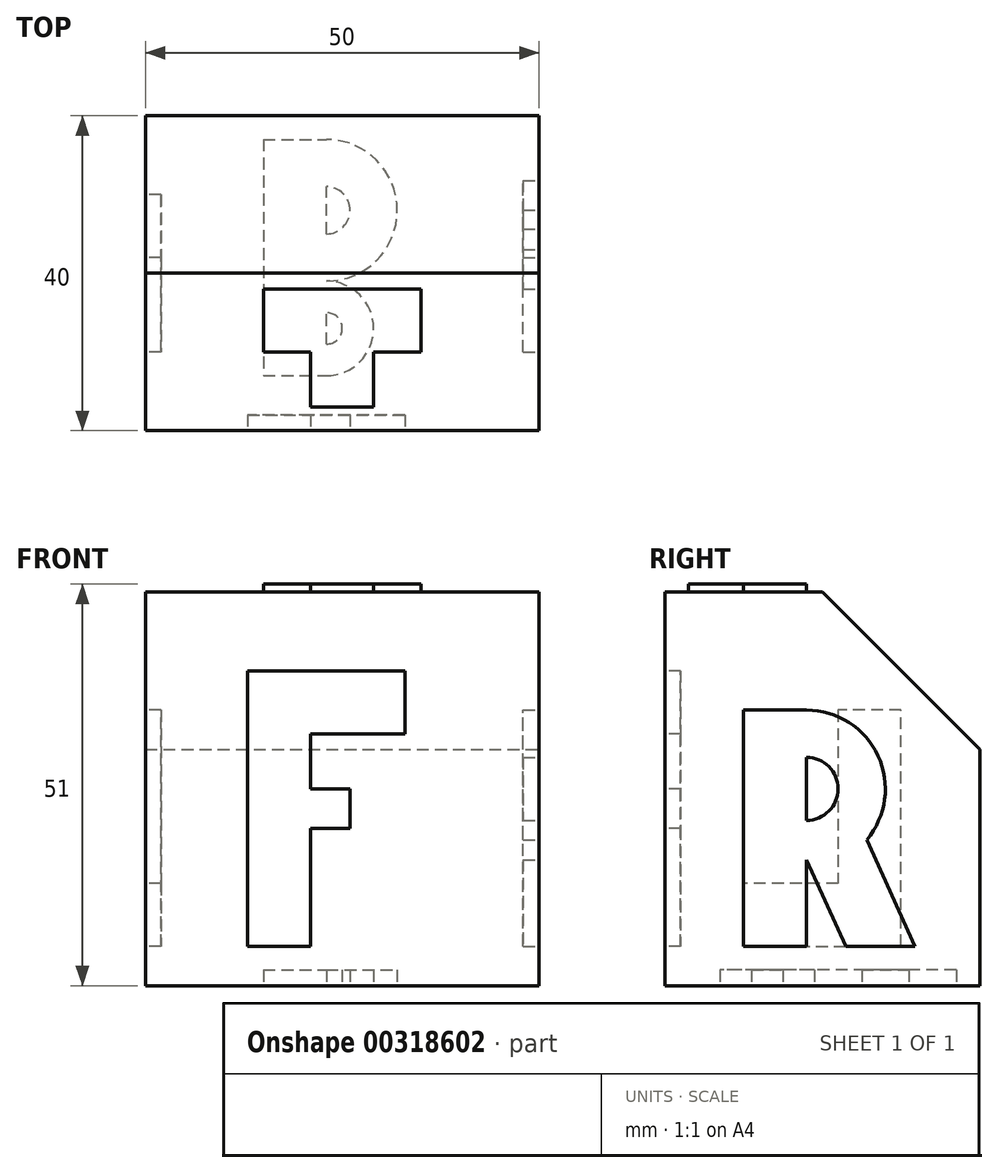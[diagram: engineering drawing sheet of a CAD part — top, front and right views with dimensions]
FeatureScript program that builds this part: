
annotation { "Feature Type Name" : "Feature", "Feature Type Description" : "" }
export const myFeature = defineFeature(function(context is Context, id is Id, definition is map)
    precondition{}
    {
        {
            var Q0;
            Q0=qCreatedBy(makeId("Front.planeOp"),FACE);
            var sketch = newSketch(context, id + "F0", { "sketchPlane" : qUnion([Q0])});
            skLineSegment(sketch, "E0", {"start": v(0, 0) * mm, "end": v(-50, 0) * mm});
            skLineSegment(sketch, "E1", {"start": v(-50, 0) * mm, "end": v(-50, 50) * mm});
            skLineSegment(sketch, "E2", {"start": v(-50, 50) * mm, "end": v(0, 50) * mm});
            skLineSegment(sketch, "E3", {"start": v(0, 50) * mm, "end": v(0, 0) * mm});
            skSolve(sketch);
        }
        {
            var Q0;
            Q0=makeQuery(id+"F0.imprint","IMPRINT",FACE,{"disambiguationData":[TD([[makeQuery(id+"F0.imprint","IMPRINT",EDGE,{"derivedFrom":sQuery(id+"F0.wireOp",EDGE,"E0")}),-1.0]])]});
            extrude(context, id + "F1", {"entities" : qUnion([Q0]), "oppositeDirection" : true, "depth" : 40 * mm});
        }
        {
            var Q0;
            Q0=makeQuery(id+"F1.opExtrude","CAP_EDGE",EDGE,{"disambiguationData":[OSD([sQuery(id+"F0.wireOp",EDGE,"E2")])],"isStart":false});
            chamfer(context, id + "F2", {"entities" : qUnion([Q0]), "width" : 20 * mm, "tangentPropagation" : true});
        }
        {
            var Q0;
            Q0=makeQuery(id+"F1.opExtrude","CAP_FACE",FACE,{"disambiguationData":[OSD([sQuery(id+"F0.wireOp",EDGE,"E0"),sQuery(id+"F0.wireOp",EDGE,"E1"),sQuery(id+"F0.wireOp",EDGE,"E2"),sQuery(id+"F0.wireOp",EDGE,"E3")])],"isStart":true});
            var sketch = newSketch(context, id + "F3", { "sketchPlane" : qUnion([Q0])});
            skLineSegment(sketch, "E4", {"start": v(-50, 5) * mm, "end": v(0, 5) * mm, "construction": true});
            skLineSegment(sketch, "E5", {"start": v(-37, 5) * mm, "end": v(-37, 40) * mm});
            skLineSegment(sketch, "E6", {"start": v(-37, 40) * mm, "end": v(-17, 40) * mm});
            skLineSegment(sketch, "E7", {"start": v(-17, 40) * mm, "end": v(-17, 32) * mm});
            skLineSegment(sketch, "E8", {"start": v(-17, 32) * mm, "end": v(-29, 32) * mm});
            skLineSegment(sketch, "E9", {"start": v(-29, 32) * mm, "end": v(-29, 25) * mm});
            skLineSegment(sketch, "E10", {"start": v(-29, 25) * mm, "end": v(-24, 25) * mm});
            skLineSegment(sketch, "E11", {"start": v(-24, 25) * mm, "end": v(-24, 20) * mm});
            skLineSegment(sketch, "E12", {"start": v(-24, 20) * mm, "end": v(-29, 20) * mm});
            skLineSegment(sketch, "E13", {"start": v(-29, 20) * mm, "end": v(-29, 5) * mm});
            skLineSegment(sketch, "E14", {"start": v(-29, 5) * mm, "end": v(-37, 5) * mm});
            skSolve(sketch);
        }
        {
            var Q0;
            Q0=makeQuery(id+"F3.imprint","IMPRINT",FACE,{"disambiguationData":[TD([[makeQuery(id+"F3.imprint","IMPRINT",EDGE,{"derivedFrom":sQuery(id+"F3.wireOp",EDGE,"E5")}),-1.0]])]});
            extrude(context, id + "F4", {"entities" : qUnion([Q0]), "operationType" : NewBodyOperationType.REMOVE, "oppositeDirection" : true, "depth" : 2 * mm});
        }
        {
            var Q0;
            Q0=makeQuery(id+"F1.opExtrude","SWEPT_FACE",FACE,{"disambiguationData":[OSD([sQuery(id+"F0.wireOp",EDGE,"E3")])]});
            var sketch = newSketch(context, id + "F5", { "sketchPlane" : qUnion([Q0])});
            skLineSegment(sketch, "E15", {"start": v(0, 5) * mm, "end": v(40, 5) * mm, "construction": true});
            skLineSegment(sketch, "E16", {"start": v(10, 5) * mm, "end": v(10, 35) * mm});
            skLineSegment(sketch, "E17", {"start": v(10, 35) * mm, "end": v(18, 35) * mm});
            skLineSegment(sketch, "E18", {"start": v(18, 29) * mm, "end": v(18, 21) * mm});
            skLineSegment(sketch, "E19", {"start": v(18, 5) * mm, "end": v(10, 5) * mm});
            skArc(sketch, "E20", {"start": v(25.63, 18.54) * mm, "mid": v(27.07, 29.2) * mm, "end": v(18, 35) * mm});
            skLineSegment(sketch, "E21", {"start": v(18, 16) * mm, "end": v(23, 5) * mm});
            skLineSegment(sketch, "E22", {"start": v(23, 5) * mm, "end": v(31.79, 5) * mm});
            skLineSegment(sketch, "E23", {"start": v(31.79, 5) * mm, "end": v(25.63, 18.54) * mm});
            skLineSegment(sketch, "E24", {"start": v(20.5, 10.5) * mm, "end": v(27.78, 13.81) * mm, "construction": true});
            skArc(sketch, "E25", {"start": v(18, 21) * mm, "mid": v(22, 25) * mm, "end": v(18, 29) * mm});
            skLineSegment(sketch, "E26.trimOffspring", {"start": v(18, 16) * mm, "end": v(18, 5) * mm});
            skSolve(sketch);
        }
        {
            var Q0;
            Q0=makeQuery(id+"F5.imprint","IMPRINT",FACE,{"disambiguationData":[TD([[makeQuery(id+"F5.imprint","IMPRINT",EDGE,{"derivedFrom":sQuery(id+"F5.wireOp",EDGE,"E16")}),-1.0]])]});
            extrude(context, id + "F6", {"entities" : qUnion([Q0]), "operationType" : NewBodyOperationType.REMOVE, "oppositeDirection" : true, "depth" : 2 * mm});
        }
        {
            var Q0;
            Q0=makeQuery(id+"F1.opExtrude","SWEPT_FACE",FACE,{"disambiguationData":[OSD([sQuery(id+"F0.wireOp",EDGE,"E1")])]});
            var sketch = newSketch(context, id + "F7", { "sketchPlane" : qUnion([Q0])});
            skLineSegment(sketch, "E27", {"start": v(-30, 35) * mm, "end": v(-22, 35) * mm});
            skLineSegment(sketch, "E28", {"start": v(-22, 35) * mm, "end": v(-22, 13) * mm});
            skLineSegment(sketch, "E29", {"start": v(-22, 13) * mm, "end": v(-10, 13) * mm});
            skLineSegment(sketch, "E30", {"start": v(-10, 13) * mm, "end": v(-10, 5) * mm});
            skLineSegment(sketch, "E31", {"start": v(-10, 5) * mm, "end": v(-30, 5) * mm});
            skLineSegment(sketch, "E32", {"start": v(-30, 5) * mm, "end": v(-30, 35) * mm});
            skSolve(sketch);
        }
        {
            var Q0;
            Q0=makeQuery(id+"F7.imprint","IMPRINT",FACE,{"disambiguationData":[TD([[makeQuery(id+"F7.imprint","IMPRINT",EDGE,{"derivedFrom":sQuery(id+"F7.wireOp",EDGE,"E27")}),-1.0]])]});
            extrude(context, id + "F8", {"entities" : qUnion([Q0]), "operationType" : NewBodyOperationType.REMOVE, "oppositeDirection" : true, "depth" : 2 * mm});
        }
        {
            var Q0;
            Q0=makeQuery(id+"F1.opExtrude","SWEPT_FACE",FACE,{"disambiguationData":[OSD([sQuery(id+"F0.wireOp",EDGE,"E2")])]});
            var sketch = newSketch(context, id + "F9", { "sketchPlane" : qUnion([Q0])});
            skLineSegment(sketch, "E33", {"start": v(-29, 3) * mm, "end": v(-29, 10) * mm});
            skLineSegment(sketch, "E34", {"start": v(-29, 10) * mm, "end": v(-35, 10) * mm});
            skLineSegment(sketch, "E35", {"start": v(-35, 10) * mm, "end": v(-35, 18) * mm});
            skLineSegment(sketch, "E36", {"start": v(-35, 18) * mm, "end": v(-15, 18) * mm});
            skLineSegment(sketch, "E37", {"start": v(-15, 18) * mm, "end": v(-15, 10) * mm});
            skLineSegment(sketch, "E38", {"start": v(-15, 10) * mm, "end": v(-21, 10) * mm});
            skLineSegment(sketch, "E39", {"start": v(-21, 10) * mm, "end": v(-21, 3) * mm});
            skLineSegment(sketch, "E40", {"start": v(-21, 3) * mm, "end": v(-29, 3) * mm});
            skSolve(sketch);
        }
        {
            var Q0;
            Q0=makeQuery(id+"F9.imprint","IMPRINT",FACE,{"disambiguationData":[TD([[makeQuery(id+"F9.imprint","IMPRINT",EDGE,{"derivedFrom":sQuery(id+"F9.wireOp",EDGE,"E33")}),-1.0]])]});
            extrude(context, id + "F10", {"entities" : qUnion([Q0]), "operationType" : NewBodyOperationType.ADD, "depth" : 1 * mm});
        }
        {
            var Q0;
            Q0=makeQuery(id+"F1.opExtrude","SWEPT_FACE",FACE,{"disambiguationData":[OSD([sQuery(id+"F0.wireOp",EDGE,"E0")])]});
            var sketch = newSketch(context, id + "F11", { "sketchPlane" : qUnion([Q0])});
            skLineSegment(sketch, "E41", {"start": v(-35, -37) * mm, "end": v(-35, -7) * mm});
            skLineSegment(sketch, "E42", {"start": v(-35, -7) * mm, "end": v(-27, -7) * mm});
            skLineSegment(sketch, "E43", {"start": v(-35, -37) * mm, "end": v(-27, -37) * mm});
            skArc(sketch, "E44", {"start": v(-27, -19) * mm, "mid": v(-21, -13) * mm, "end": v(-27, -7) * mm});
            skArc(sketch, "E45", {"start": v(-27, -37) * mm, "mid": v(-18, -28) * mm, "end": v(-27, -19) * mm});
            skLineSegment(sketch, "E46", {"start": v(-27, -11) * mm, "end": v(-27, -15) * mm});
            skArc(sketch, "E47", {"start": v(-27, -15) * mm, "mid": v(-25, -13) * mm, "end": v(-27, -11) * mm});
            skArc(sketch, "E48", {"start": v(-27, -31) * mm, "mid": v(-24, -28) * mm, "end": v(-27, -25) * mm});
            skLineSegment(sketch, "E49.trimOffspring", {"start": v(-27, -25) * mm, "end": v(-27, -31) * mm});
            skSolve(sketch);
        }
        {
            var Q0;
            Q0=makeQuery(id+"F11.imprint","IMPRINT",FACE,{"disambiguationData":[TD([[makeQuery(id+"F11.imprint","IMPRINT",EDGE,{"derivedFrom":sQuery(id+"F11.wireOp",EDGE,"E41")}),-1.0]])]});
            extrude(context, id + "F12", {"entities" : qUnion([Q0]), "operationType" : NewBodyOperationType.REMOVE, "oppositeDirection" : true, "depth" : 2 * mm});
        }
    });
